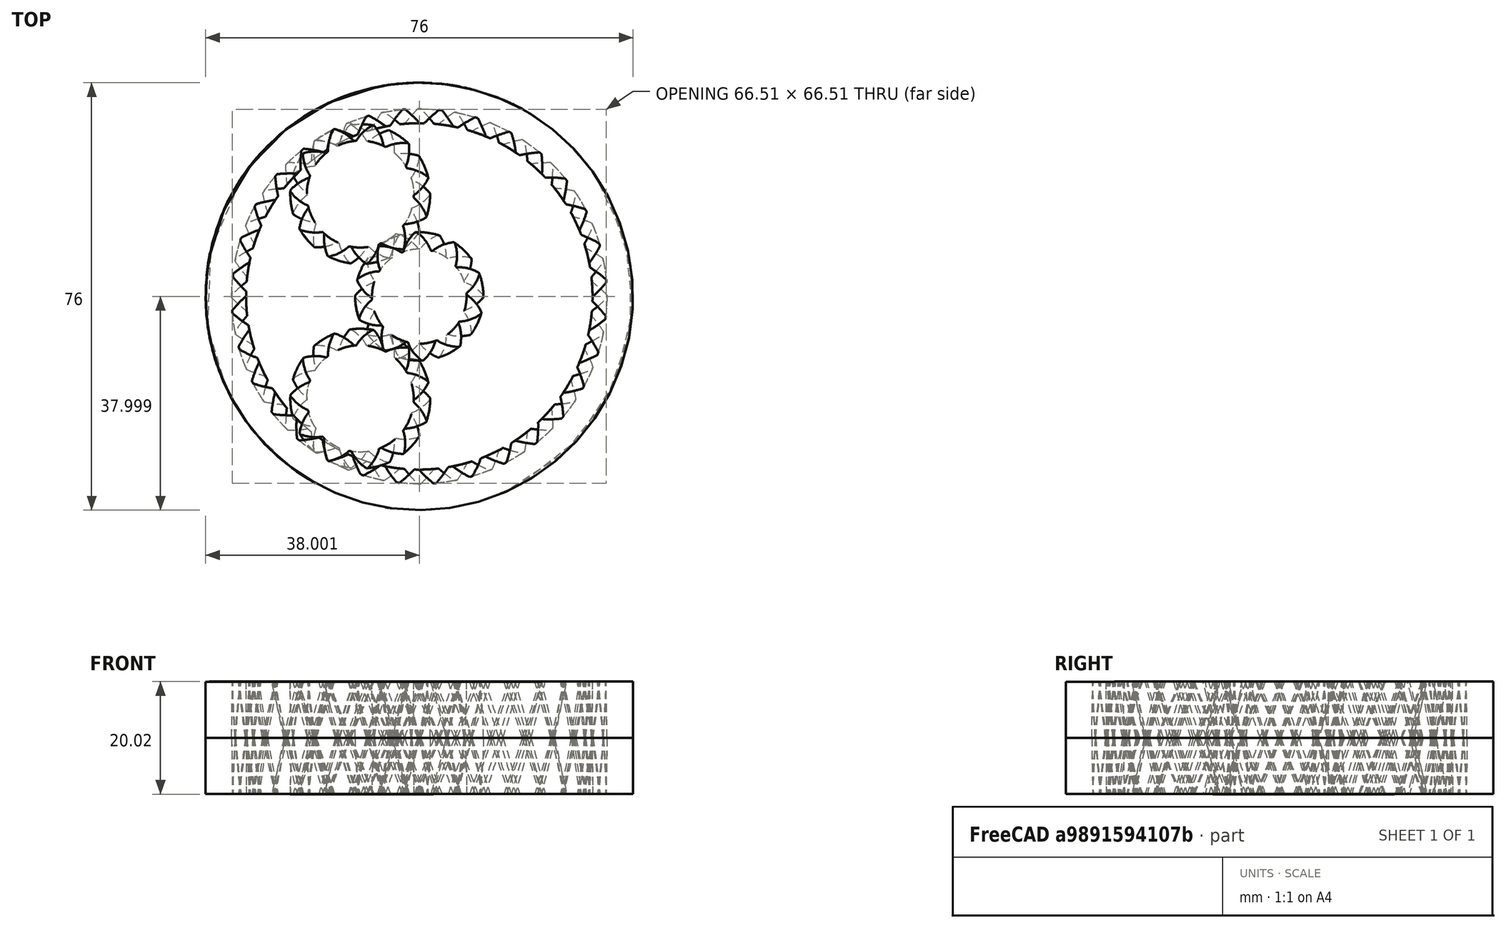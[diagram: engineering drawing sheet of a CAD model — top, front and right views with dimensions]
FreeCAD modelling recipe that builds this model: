
FCSTD DOCUMENT  (FreeCAD 0.20R29603 (Git))
Label: model
License: All rights reserved
LicenseURL: http://en.wikipedia.org/wiki/All_rights_reserved
objects: Part::FeaturePython×3, PartDesign::FeatureBase×2, PartDesign::Body×2, Mesh::Feature×1
note: 7 computed .brp shape members not serialized (recipe doc carries the construction recipe); baked Part::Feature solids carry a one-line shape summary decoded from their .brp

FEATURE [Part::FeaturePython] InvoluteGear  label="InputSunGear"  # WARN: FeaturePython — macro-defined, semantics opaque (R4)
  AttacherType = Attacher::AttachEngine3D
  angular_backlash = 0
  backlash = 0
  beta = 20
  clearance = 0.25
  da = 24
  df = 15
  double_helix = true
  dw = 20
  head = 0
  head_fillet = 0
  height = 20
  module = 2
  numpoints = 11
  pressure_angle = 44
  properties_from_tool = false
  reversed_backlash = false
  root_fillet = 0
  shift = 0
  simple = false
  teeth = 10
  transverse_pitch = 6.28319
  traverse_module = 2
  undercut = false
  version = 0.0.4
  expr: angular_backlash = backlash / dw * 360 ° / pi
FEATURE [Part::FeaturePython] InvoluteGear001  label="InputPlanetGear001"  # WARN: FeaturePython — macro-defined, semantics opaque (R4)
  AttacherType = Attacher::AttachEngine3D
  Placement = pos=(21,0,0) rot=(0,0,1;3.42719rad)
  angular_backlash = 0
  backlash = 0
  beta = -20
  clearance = 0.25
  da = 26
  df = 17
  double_helix = true
  dw = 22
  head = 0
  head_fillet = 0
  height = 20
  module = 2
  numpoints = 11
  pressure_angle = 44
  properties_from_tool = false
  reversed_backlash = false
  root_fillet = 0
  shift = 0
  simple = false
  teeth = 11
  transverse_pitch = 6.28319
  traverse_module = 2
  undercut = false
  version = 0.0.4
  expr: .Placement.Base.x = (dw + <<InputSunGear>>.dw) / 2
  expr: .Placement.Rotation.Angle = 180 / teeth + 180
  expr: angular_backlash = backlash / dw * 360 ° / pi
  expr: beta = -<<InputSunGear>>.beta
  expr: height = <<InputSunGear>>.height
  expr: module = <<InputSunGear>>.module
  expr: pressure_angle = <<InputSunGear>>.pressure_angle
FEATURE [PartDesign::FeatureBase] Clone
  BaseFeature = -> InvoluteGear001
  Placement = pos=(21,0,0) rot=(0,0,1;5.33119rad)
  expr: .Placement.Base.x = (<<InputPlanetGear001>>.dw + <<InputSunGear>>.dw) / 2
  expr: .Placement.Rotation.Angle = 180 / <<InputPlanetGear001>>.teeth + 180 + (120 - 0) * <<InputSunGear>>.teeth / <<InputPlanetGear001>>.teeth
FEATURE [PartDesign::Body] Body
  BaseFeature = -> InvoluteGear001
  Group = -> [Clone]
  Origin = -> Origin
  Placement = pos=(0,0,0) rot=(0,0,1;2.0944rad)
  Tip = -> Clone
  expr: .Placement.Rotation.Angle = 120
FEATURE [PartDesign::FeatureBase] Clone001
  BaseFeature = -> InvoluteGear001
  Placement = pos=(21,0,0) rot=(0,0,1;7.23518rad)
  expr: .Placement.Base.x = (<<InputPlanetGear001>>.dw + <<InputSunGear>>.dw) / 2
  expr: .Placement.Rotation.Angle = 180 / <<InputPlanetGear001>>.teeth + 180 + (240 - 0) * <<InputSunGear>>.teeth / <<InputPlanetGear001>>.teeth
FEATURE [PartDesign::Body] Body001
  BaseFeature = -> InvoluteGear001
  Group = -> [Clone001]
  Origin = -> Origin001
  Placement = pos=(0,0,0) rot=(0,0,1;4.18879rad)
  Tip = -> Clone001
FEATURE [Part::FeaturePython] InternalInvoluteGear  label="InputRing"  # WARN: FeaturePython — macro-defined, semantics opaque (R4)
  AttacherType = Attacher::AttachEngine3D
  Placement = pos=(0,0,0) rot=(0,0,1;1.1781rad)
  angular_backlash = 0
  backlash = 0
  beta = -20
  clearance = 0.25
  da = 61.6
  df = 69
  double_helix = true
  dw = 64
  head = -0.4
  head_fillet = 0
  height = 20
  module = 2
  numpoints = 11
  outside_diameter = 76
  pressure_angle = 44
  properties_from_tool = false
  reversed_backlash = false
  root_fillet = 0
  shift = 0
  simple = false
  teeth = 32
  thickness = 6
  transverse_pitch = 6.28319
  version = 0.0.4
  expr: .Placement.Rotation.Angle = 180 / teeth * (1 + <<InputPlanetGear001>>.teeth)
  expr: angular_backlash = backlash / dw * 360 ° / pi
  expr: beta = -<<InputSunGear>>.beta
  expr: height = <<InputSunGear>>.height
  expr: module = <<InputSunGear>>.module
  expr: pressure_angle = <<InputSunGear>>.pressure_angle
  expr: teeth = <<InputSunGear>>.teeth + <<InputPlanetGear001>>.teeth * 2
FEATURE [Mesh::Feature] ringgeartest_distorted
